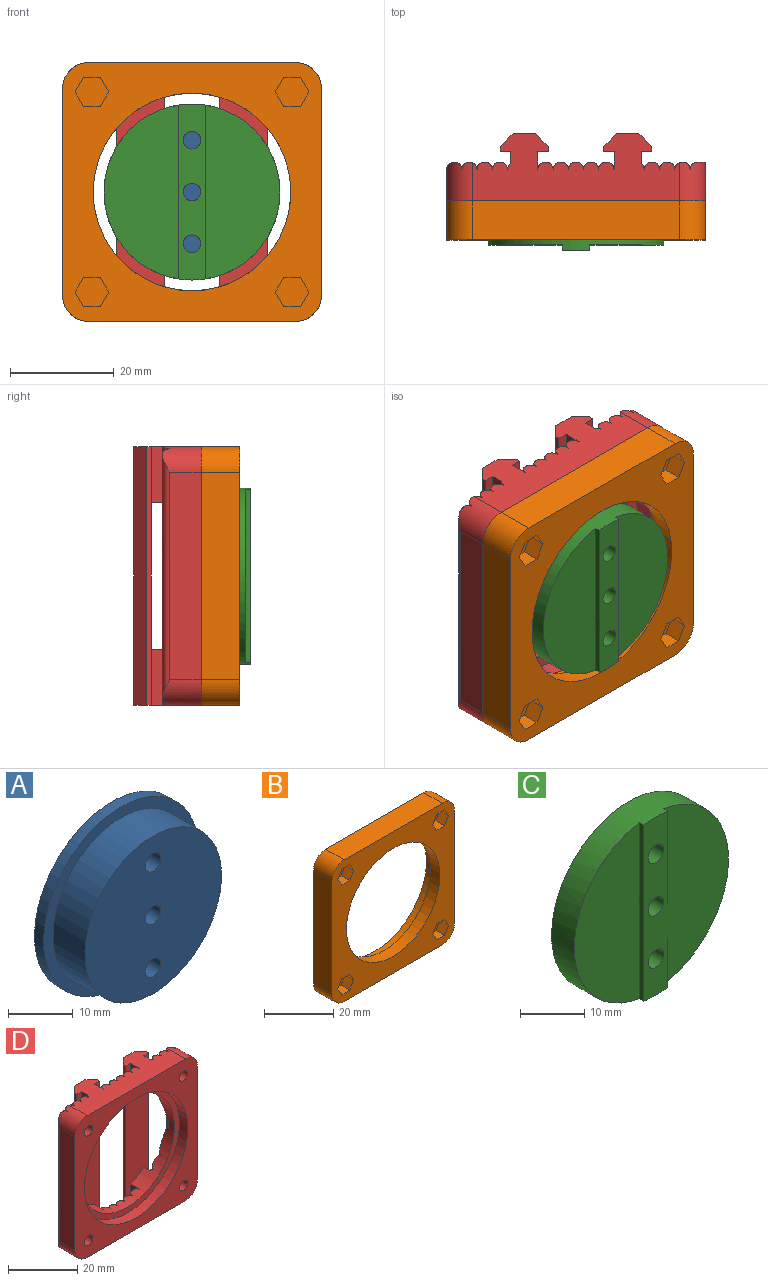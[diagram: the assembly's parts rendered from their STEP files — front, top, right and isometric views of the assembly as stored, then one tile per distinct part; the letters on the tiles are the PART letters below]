
ASSEMBLY  parts=4 mates=3
PART A: 17 faces, bbox 34x9x34 mm
  f0: cylinder r=1.7mm len=5.8mm, axis (0,1,0), area 62mm2, adj f7,f16
  f1: cylinder r=1.7mm len=5.8mm, axis (0,1,0), area 62mm2, adj f7,f15
  f2: cylinder r=1.7mm len=5.8mm, axis (0,1,0), area 62mm2, adj f7,f14
  f3: cylinder r=17mm len=34mm, axis (0,1,0), area 213.6mm2, adj f4,f5
  f4: plane 34x34mm, normal (0,-1,0), area 205.8mm2, adj f3,f6
  f5: plane 34x34mm, normal (0,1,0), area 808.4mm2, adj f3,f9,f11,f13
  f6: cylinder r=14.95mm len=29.9mm, axis (0,1,0), area 657.5mm2, adj f4,f7
  f7: plane 29.9x29.9mm, normal (0,-1,0), area 674.9mm2, adj f0,f1,f2,f6
  f8: plane 6.5x6.5mm, normal (0,1,0), area 33.2mm2, adj f9
  f9: cylinder r=3.25mm len=6.5mm, axis (0,1,0), area 61.3mm2, adj f5,f8
  f10: plane 6.5x6.5mm, normal (0,1,0), area 33.2mm2, adj f11
  f11: cylinder r=3.25mm len=6.5mm, axis (0,1,0), area 61.3mm2, adj f5,f10
  f12: plane 6.5x6.5mm, normal (0,1,0), area 33.2mm2, adj f13
  f13: cylinder r=3.25mm len=6.5mm, axis (0,1,0), area 61.3mm2, adj f5,f12
  f14: plane 3.4x3.4mm, normal (0,-1,0), area 9.1mm2, adj f2
  f15: plane 3.4x3.4mm, normal (0,-1,0), area 9.1mm2, adj f1
  f16: plane 3.4x3.4mm, normal (0,-1,0), area 9.1mm2, adj f0
PART B: 49 faces, bbox 50x7.5x50 mm
  f0: cylinder r=1.7mm len=3.8mm, axis (0,-1,0), area 40.6mm2, adj f9,f48
  f1: cylinder r=1.7mm len=3.8mm, axis (0,-1,0), area 40.6mm2, adj f9,f47
  f2: cylinder r=1.7mm len=3.8mm, axis (0,-1,0), area 40.6mm2, adj f9,f46
  f3: cylinder r=1.7mm len=3.8mm, axis (0,-1,0), area 40.6mm2, adj f9,f45
  f4: cylinder r=21.07mm len=42.15mm, axis (0,-1,0), area 476.7mm2, adj f9,f12
  f5: plane 40x7.5mm, normal (0,0,1), area 300mm2, adj f9,f10,f13,f16
  f6: plane 40x7.5mm, normal (-1,0,0), area 300mm2, adj f9,f10,f13,f14
  f7: plane 40x7.5mm, normal (0,0,-1), area 300mm2, adj f9,f10,f14,f15
  f8: plane 40x7.5mm, normal (1,0,0), area 300mm2, adj f9,f10,f15,f16
  f9: plane 50x50mm, normal (0,1,0), area 1046.9mm2, adj f0,f1,f2,f3,f4,f5,f6,f7
  f10: plane 50x50mm, normal (0,-1,0), area 1225.7mm2, adj f5,f6,f7,f8,f11,f13,f14,f15
  f11: cylinder r=19.08mm len=38.15mm, axis (0,-1,0), area 467.4mm2, adj f10,f12
  f12: plane 42.15x42.15mm, normal (0,1,0), area 252.3mm2, adj f4,f11
  f13: cylinder r=5mm len=7.5mm, axis (0,1,0), area 58.9mm2, adj f5,f6,f9,f10
  f14: cylinder r=5mm len=7.5mm, axis (0,-1,0), area 58.9mm2, adj f6,f7,f9,f10
  f15: cylinder r=5mm len=7.5mm, axis (0,1,0), area 58.9mm2, adj f7,f8,f9,f10
  f16: cylinder r=5mm len=7.5mm, axis (0,-1,0), area 58.9mm2, adj f5,f8,f9,f10
  f17: plane 3.5x2.81mm, normal (-0.87,0,-0.5), area 11.4mm2, adj f10,f18,f22,f23
  f18: plane 3.5x3.25mm, normal (0,0,-1), area 11.4mm2, adj f10,f17,f19,f23
  f19: plane 3.5x2.81mm, normal (0.87,0,-0.5), area 11.4mm2, adj f10,f18,f20,f23
  f20: plane 3.5x2.81mm, normal (0.87,0,0.5), area 11.4mm2, adj f10,f19,f21,f23
  f21: plane 3.5x3.25mm, normal (0,0,1), area 11.4mm2, adj f10,f20,f22,f23
  f22: plane 3.5x2.81mm, normal (-0.87,0,0.5), area 11.4mm2, adj f10,f17,f21,f23
  f23: plane 6.5x5.63mm, normal (0,-1,0), area 27.4mm2, adj f17,f18,f19,f20,f21,f22
  f24: plane 3.5x3.25mm, normal (0,0,-1), area 11.4mm2, adj f10,f25,f29,f30
  f25: plane 3.5x2.81mm, normal (0.87,0,-0.5), area 11.4mm2, adj f10,f24,f26,f30
  f26: plane 3.5x2.81mm, normal (0.87,0,0.5), area 11.4mm2, adj f10,f25,f27,f30
  f27: plane 3.5x3.25mm, normal (0,0,1), area 11.4mm2, adj f10,f26,f28,f30
  f28: plane 3.5x2.81mm, normal (-0.87,0,0.5), area 11.4mm2, adj f10,f27,f29,f30
  f29: plane 3.5x2.81mm, normal (-0.87,0,-0.5), area 11.4mm2, adj f10,f24,f28,f30
  f30: plane 6.5x5.63mm, normal (0,-1,0), area 27.4mm2, adj f24,f25,f26,f27,f28,f29
  f31: plane 3.5x3.25mm, normal (0,0,-1), area 11.4mm2, adj f10,f32,f36,f37
  f32: plane 3.5x2.81mm, normal (0.87,0,-0.5), area 11.4mm2, adj f10,f31,f33,f37
  f33: plane 3.5x2.81mm, normal (0.87,0,0.5), area 11.4mm2, adj f10,f32,f34,f37
  f34: plane 3.5x3.25mm, normal (0,0,1), area 11.4mm2, adj f10,f33,f35,f37
  f35: plane 3.5x2.81mm, normal (-0.87,0,0.5), area 11.4mm2, adj f10,f34,f36,f37
  f36: plane 3.5x2.81mm, normal (-0.87,0,-0.5), area 11.4mm2, adj f10,f31,f35,f37
  f37: plane 6.5x5.63mm, normal (0,-1,0), area 27.4mm2, adj f31,f32,f33,f34,f35,f36
  f38: plane 3.5x3.25mm, normal (0,0,1), area 11.4mm2, adj f10,f39,f43,f44
  f39: plane 3.5x2.81mm, normal (-0.87,0,0.5), area 11.4mm2, adj f10,f38,f40,f44
  f40: plane 3.5x2.81mm, normal (-0.87,0,-0.5), area 11.4mm2, adj f10,f39,f41,f44
  f41: plane 3.5x3.25mm, normal (0,0,-1), area 11.4mm2, adj f10,f40,f42,f44
  f42: plane 3.5x2.81mm, normal (0.87,0,-0.5), area 11.4mm2, adj f10,f41,f43,f44
  f43: plane 3.5x2.81mm, normal (0.87,0,0.5), area 11.4mm2, adj f10,f38,f42,f44
  f44: plane 6.5x5.63mm, normal (0,-1,0), area 27.4mm2, adj f38,f39,f40,f41,f42,f43
  f45: plane 3.4x3.4mm, normal (0,1,0), area 9.1mm2, adj f3
  f46: plane 3.4x3.4mm, normal (0,1,0), area 9.1mm2, adj f2
  f47: plane 3.4x3.4mm, normal (0,1,0), area 9.1mm2, adj f1
  f48: plane 3.4x3.4mm, normal (0,1,0), area 9.1mm2, adj f0
PART C: 10 faces, bbox 34x6x34 mm
  f0: plane 33.58x14.35mm, normal (0,-1,0), area 364.2mm2, adj f4,f8
  f1: cylinder r=1.7mm len=6mm, axis (0,-1,0), area 64.1mm2, adj f5,f9
  f2: cylinder r=1.7mm len=6mm, axis (0,-1,0), area 64.1mm2, adj f5,f9
  f3: cylinder r=1.7mm len=6mm, axis (0,-1,0), area 64.1mm2, adj f5,f9
  f4: cylinder r=17mm len=34mm, axis (0,-1,0), area 544.7mm2, adj f0,f5,f6,f7,f8,f9
  f5: plane 34x34mm, normal (0,1,0), area 880.7mm2, adj f1,f2,f3,f4
  f6: plane 33.58x14.35mm, normal (0,-1,0), area 364.2mm2, adj f4,f7
  f7: plane 33.58x1mm, normal (-1,0,0), area 33.6mm2, adj f4,f6,f9
  f8: plane 33.58x1mm, normal (1,0,0), area 33.6mm2, adj f0,f4,f9
  f9: plane 34x5.3mm, normal (0,-1,0), area 152.2mm2, adj f1,f2,f3,f4,f7,f8
PART D: 81 faces, bbox 50x13x50 mm
  f0: plane 40x13mm, normal (0,0,1), area 363mm2, adj f6,f9,f12,f15,f16,f18,f35,f37
  f1: plane 40x13mm, normal (0,0,-1), area 363mm2, adj f2,f3,f5,f8,f11,f14,f20,f21
  f2: cylinder r=1.47mm len=14.9mm, axis (0,0,-1), area 59.3mm2, adj f1,f13,f14,f28,f65,f75
  f3: cylinder r=1.47mm len=14.87mm, axis (0,0,-1), area 59.3mm2, adj f1,f4,f5,f32,f65,f78
  f4: cylinder r=1.47mm len=37.37mm, axis (0,0,-1), area 96.9mm2, adj f3,f7,f18,f65,f69,f78
  f5: cylinder r=1.47mm len=5mm, axis (0,0,-1), area 15mm2, adj f1,f3,f8,f78
  f6: cylinder r=1.47mm len=5mm, axis (0,0,-1), area 15mm2, adj f0,f9,f18,f69
  f7: cylinder r=1.47mm len=35.06mm, axis (0,0,-1), area 153mm2, adj f4,f19,f69,f78
  f8: cylinder r=1.47mm len=3.84mm, axis (0,0,-1), area 12.7mm2, adj f1,f5,f19,f34,f78
  f9: cylinder r=1.47mm len=3.84mm, axis (0,0,-1), area 12.7mm2, adj f0,f6,f19,f35,f69
  f10: cylinder r=1.47mm len=35.12mm, axis (0,0,-1), area 153.1mm2, adj f13,f17,f72,f75
  f11: cylinder r=1.47mm len=3.87mm, axis (0,0,-1), area 12.7mm2, adj f1,f14,f17,f36,f75
  f12: cylinder r=1.47mm len=3.87mm, axis (0,0,-1), area 12.7mm2, adj f0,f15,f17,f37,f72
  f13: cylinder r=1.47mm len=37.19mm, axis (0,0,-1), area 97.4mm2, adj f2,f10,f16,f65,f72,f75
  f14: cylinder r=1.47mm len=4.91mm, axis (0,0,-1), area 14.9mm2, adj f1,f2,f11,f75
  f15: cylinder r=1.47mm len=4.91mm, axis (0,0,-1), area 14.9mm2, adj f0,f12,f16,f72
  f16: cylinder r=1.47mm len=14.9mm, axis (0,0,-1), area 59.3mm2, adj f0,f13,f15,f58,f65,f72
  f17: cylinder r=1.47mm len=49.11mm, axis (0,0,-1), area 206mm2, adj f10,f11,f12,f36,f37,f38,f72,f75
  f18: cylinder r=1.47mm len=14.87mm, axis (0,0,-1), area 59.3mm2, adj f0,f4,f6,f62,f65,f69
  f19: cylinder r=1.47mm len=49.13mm, axis (0,0,-1), area 104.5mm2, adj f7,f8,f9,f33,f34,f35,f69,f78
  f20: plane 10.72x2.39mm, normal (-1,0,0), area 25.7mm2, adj f1,f28,f65,f80
  f21: plane 7.4x2.1mm, normal (1,0,0), area 15.5mm2, adj f1,f31,f65,f80
  f22: plane 7.4x2.1mm, normal (-1,0,0), area 15.5mm2, adj f1,f30,f65,f79
  f23: plane 10.72x2.41mm, normal (1,0,0), area 25.8mm2, adj f1,f32,f65,f79
  f24: cylinder r=1.47mm len=6.44mm, axis (0,0,-1), area 28.7mm2, adj f1,f25,f27,f65
  f25: cylinder r=1.47mm len=7.39mm, axis (0,0,-1), area 31.8mm2, adj f1,f24,f30,f65
  f26: cylinder r=1.47mm len=6.44mm, axis (0,0,-1), area 28.7mm2, adj f1,f27,f29,f65
  f27: cylinder r=1.47mm len=5.98mm, axis (0,0,-1), area 27.5mm2, adj f1,f24,f26,f65
  f28: cylinder r=1.47mm len=11.27mm, axis (0,0,-1), area 15.1mm2, adj f1,f2,f20,f65
  f29: cylinder r=1.47mm len=7.4mm, axis (0,0,-1), area 31.6mm2, adj f1,f26,f31,f65
  f30: plane 7.4x1.47mm, normal (-1,0.01,0), area 10.8mm2, adj f1,f22,f25,f65
  f31: plane 7.4x1.45mm, normal (1,-0.01,0), area 10.7mm2, adj f1,f21,f29,f65
  f32: cylinder r=1.47mm len=11.25mm, axis (0,0,-1), area 14.8mm2, adj f1,f3,f23,f65
  f33: plane 47.12x1.49mm, normal (0,1,0), area 66.9mm2, adj f19,f34,f35,f39
  f34: cylinder r=5mm len=7.5mm, axis (0,1,0), area 57.9mm2, adj f1,f8,f19,f33,f39,f66
  f35: cylinder r=5mm len=7.5mm, axis (0,-1,0), area 57.9mm2, adj f0,f9,f19,f33,f39,f66
  f36: cylinder r=5mm len=7.5mm, axis (0,-1,0), area 55.6mm2, adj f1,f11,f17,f38,f66
  f37: cylinder r=5mm len=7.5mm, axis (0,1,0), area 55.6mm2, adj f0,f12,f17,f38,f66
  f38: plane 40x6.03mm, normal (-1,0,0), area 241.2mm2, adj f17,f36,f37,f66
  f39: plane 40x7.5mm, normal (1,0,0), area 300mm2, adj f33,f34,f35,f66
  f40: plane 10.72x2.39mm, normal (-1,0,0), area 25.7mm2, adj f0,f58,f65,f80
  f41: plane 7.4x2.1mm, normal (1,0,0), area 15.5mm2, adj f0,f61,f65,f80
  f42: plane 7.4x2.1mm, normal (-1,0,0), area 15.5mm2, adj f0,f60,f65,f79
  f43: plane 10.72x2.41mm, normal (1,0,0), area 25.8mm2, adj f0,f62,f65,f79
  f44: plane 50x0.9mm, normal (-1,0,0), area 45mm2, adj f0,f1,f53,f80
  f45: plane 50x4.3mm, normal (0,1,0), area 215mm2, adj f0,f1,f52,f53
  f46: plane 50x0.9mm, normal (1,0,0), area 45mm2, adj f0,f1,f52,f80
  f47: plane 50x0.9mm, normal (-1,0,0), area 45mm2, adj f0,f1,f51,f79
  f48: plane 50x4.3mm, normal (0,1,0), area 215mm2, adj f0,f1,f50,f51
  f49: plane 50x0.9mm, normal (1,0,0), area 45mm2, adj f0,f1,f50,f79
  f50: plane 50x2.5mm, normal (0.71,0.71,0), area 176.8mm2, adj f0,f1,f48,f49
  f51: plane 50x2.5mm, normal (-0.71,0.71,0), area 176.8mm2, adj f0,f1,f47,f48
  f52: plane 50x2.5mm, normal (0.71,0.71,0), area 176.8mm2, adj f0,f1,f45,f46
  f53: plane 50x2.5mm, normal (-0.71,0.71,0), area 176.8mm2, adj f0,f1,f44,f45
  f54: cylinder r=1.47mm len=6.44mm, axis (0,0,-1), area 28.7mm2, adj f0,f55,f57,f65
  f55: cylinder r=1.47mm len=7.39mm, axis (0,0,-1), area 31.8mm2, adj f0,f54,f60,f65
  f56: cylinder r=1.47mm len=6.44mm, axis (0,0,-1), area 28.7mm2, adj f0,f57,f59,f65
  f57: cylinder r=1.47mm len=5.98mm, axis (0,0,-1), area 27.6mm2, adj f0,f54,f56,f65
  f58: cylinder r=1.47mm len=11.27mm, axis (0,0,-1), area 15.1mm2, adj f0,f16,f40,f65
  f59: cylinder r=1.47mm len=7.4mm, axis (0,0,-1), area 31.6mm2, adj f0,f56,f61,f65
  f60: plane 7.4x1.47mm, normal (-1,0.01,0), area 10.8mm2, adj f0,f42,f55,f65
  f61: plane 7.4x1.45mm, normal (1,-0.01,0), area 10.7mm2, adj f0,f41,f59,f65
  f62: cylinder r=1.47mm len=11.25mm, axis (0,0,-1), area 14.8mm2, adj f0,f18,f43,f65
  f63: cylinder r=21.07mm len=42.15mm, axis (0,-1,0), area 463.5mm2, adj f64,f66
  f64: plane 42.15x42.15mm, normal (0,-1,0), area 252.3mm2, adj f63,f65
  f65: cylinder r=19.08mm len=38.15mm, axis (0,-1,0), area 495.7mm2, adj f2,f3,f4,f13,f16,f18,f20,f21
  f66: plane 50x50mm, normal (0,-1,0), area 1046.9mm2, adj f0,f1,f34,f35,f36,f37,f38,f39
  f67: cylinder r=1.7mm len=3.5mm, axis (0,1,0), area 37.4mm2, adj f66,f68
  f68: plane 6.5x6.5mm, normal (0,1,0), area 24.1mm2, adj f67,f69
  f69: cylinder r=3.25mm len=6.5mm, axis (0,1,0), area 72.4mm2, adj f4,f6,f7,f9,f18,f19,f68
  f70: cylinder r=1.7mm len=3.5mm, axis (0,1,0), area 37.4mm2, adj f66,f71
  f71: plane 6.5x6.5mm, normal (0,1,0), area 24.1mm2, adj f70,f72
  f72: cylinder r=3.25mm len=6.5mm, axis (0,1,0), area 72.4mm2, adj f10,f12,f13,f15,f16,f17,f71
  f73: cylinder r=1.7mm len=3.5mm, axis (0,1,0), area 37.4mm2, adj f66,f74
  f74: plane 6.5x6.5mm, normal (0,1,0), area 24.1mm2, adj f73,f75
  f75: cylinder r=3.25mm len=6.5mm, axis (0,1,0), area 72.4mm2, adj f2,f10,f11,f13,f14,f17,f74
  f76: cylinder r=1.7mm len=3.5mm, axis (0,1,0), area 37.4mm2, adj f66,f77
  f77: plane 6.5x6.5mm, normal (0,1,0), area 24.1mm2, adj f76,f78
  f78: cylinder r=3.25mm len=6.5mm, axis (0,1,0), area 72.4mm2, adj f3,f4,f5,f7,f8,f19,f77
  f79: plane 50x9.3mm, normal (0,-1,0), area 371.1mm2, adj f0,f1,f22,f23,f42,f43,f47,f49
  f80: plane 50x9.3mm, normal (0,-1,0), area 371.1mm2, adj f0,f1,f20,f21,f40,f41,f44,f46
PLACE A t=(-11.14,80.82,-54.59)mm
PLACE B t=(-11.14,62.82,-54.59)mm
PLACE C t=(-11.14,85.82,-54.59)mm
PLACE D t=(-11.14,55.32,-54.59)mm
MATE revolute A.f1 <-> D.f63  axis (0,-1,0) through (-0.44,1.88,0.41)mm
MATE fastened B.f3 <-> D.f70  axis (0,1,0) through (-19.79,-1.62,19.75)mm
MATE fastened A.f1 <-> C.f2  axis (0,-1,0) through (-0.44,-5.12,0.41)mm
